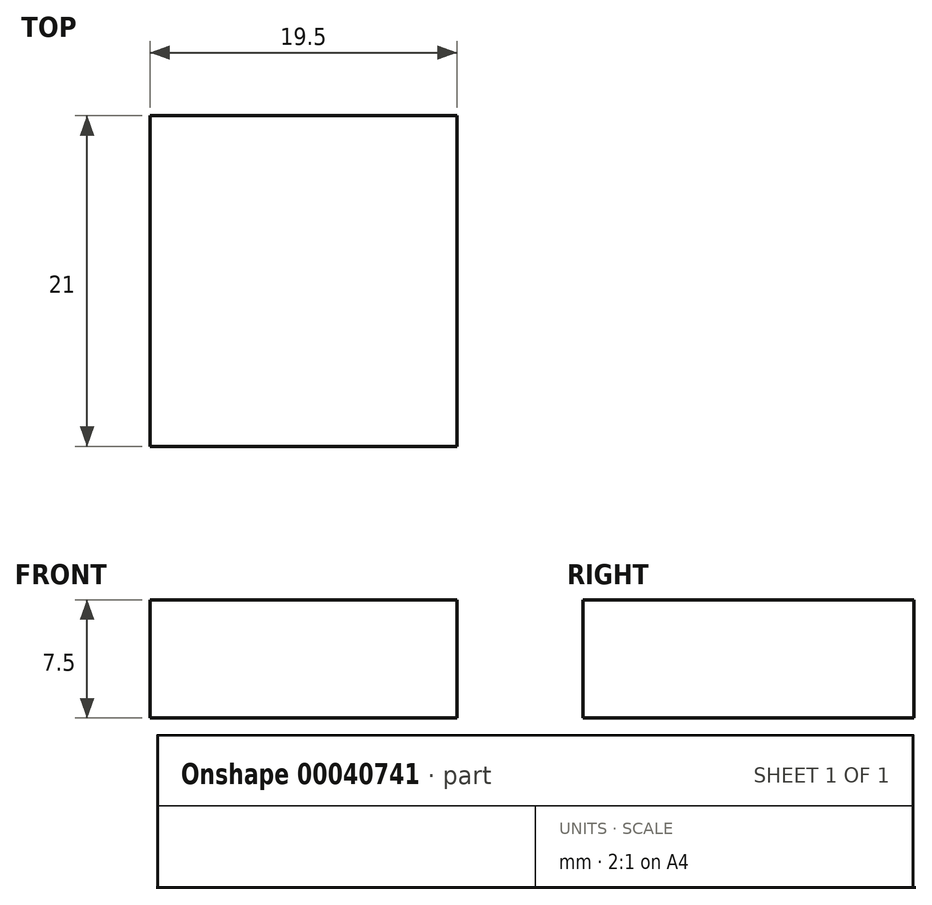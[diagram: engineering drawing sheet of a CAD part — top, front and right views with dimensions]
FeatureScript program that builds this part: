
annotation { "Feature Type Name" : "Feature", "Feature Type Description" : "" }
export const myFeature = defineFeature(function(context is Context, id is Id, definition is map)
    precondition{}
    {
        {
            var Q0;
            Q0=qCreatedBy(makeId("Top.planeOp"),FACE);
            var sketch = newSketch(context, id + "F0", { "sketchPlane" : qUnion([Q0])});
            skLineSegment(sketch, "E0.rect.bottom", {"start": v(9.75, -10.5) * mm, "end": v(-9.75, -10.5) * mm});
            skLineSegment(sketch, "E0.rect.top", {"start": v(9.75, 10.5) * mm, "end": v(-9.75, 10.5) * mm});
            skLineSegment(sketch, "E0.rect.left", {"start": v(9.75, -10.5) * mm, "end": v(9.75, 10.5) * mm});
            skLineSegment(sketch, "E0.rect.right", {"start": v(-9.75, -10.5) * mm, "end": v(-9.75, 10.5) * mm});
            skPoint(sketch, "E0.rect.middle", {"position": v(0, 0) * mm});
            skSolve(sketch);
        }
        {
            var Q0;
            Q0=makeQuery(id+"F0.imprint","IMPRINT",FACE,{"disambiguationData":[TD([[makeQuery(id+"F0.imprint","IMPRINT",EDGE,{"derivedFrom":sQuery(id+"F0.wireOp",EDGE,"E0.rect.bottom")}),-1.0]])]});
            extrude(context, id + "F1", {"entities" : qUnion([Q0]), "depth" : 7.5 * mm});
        }
    });
